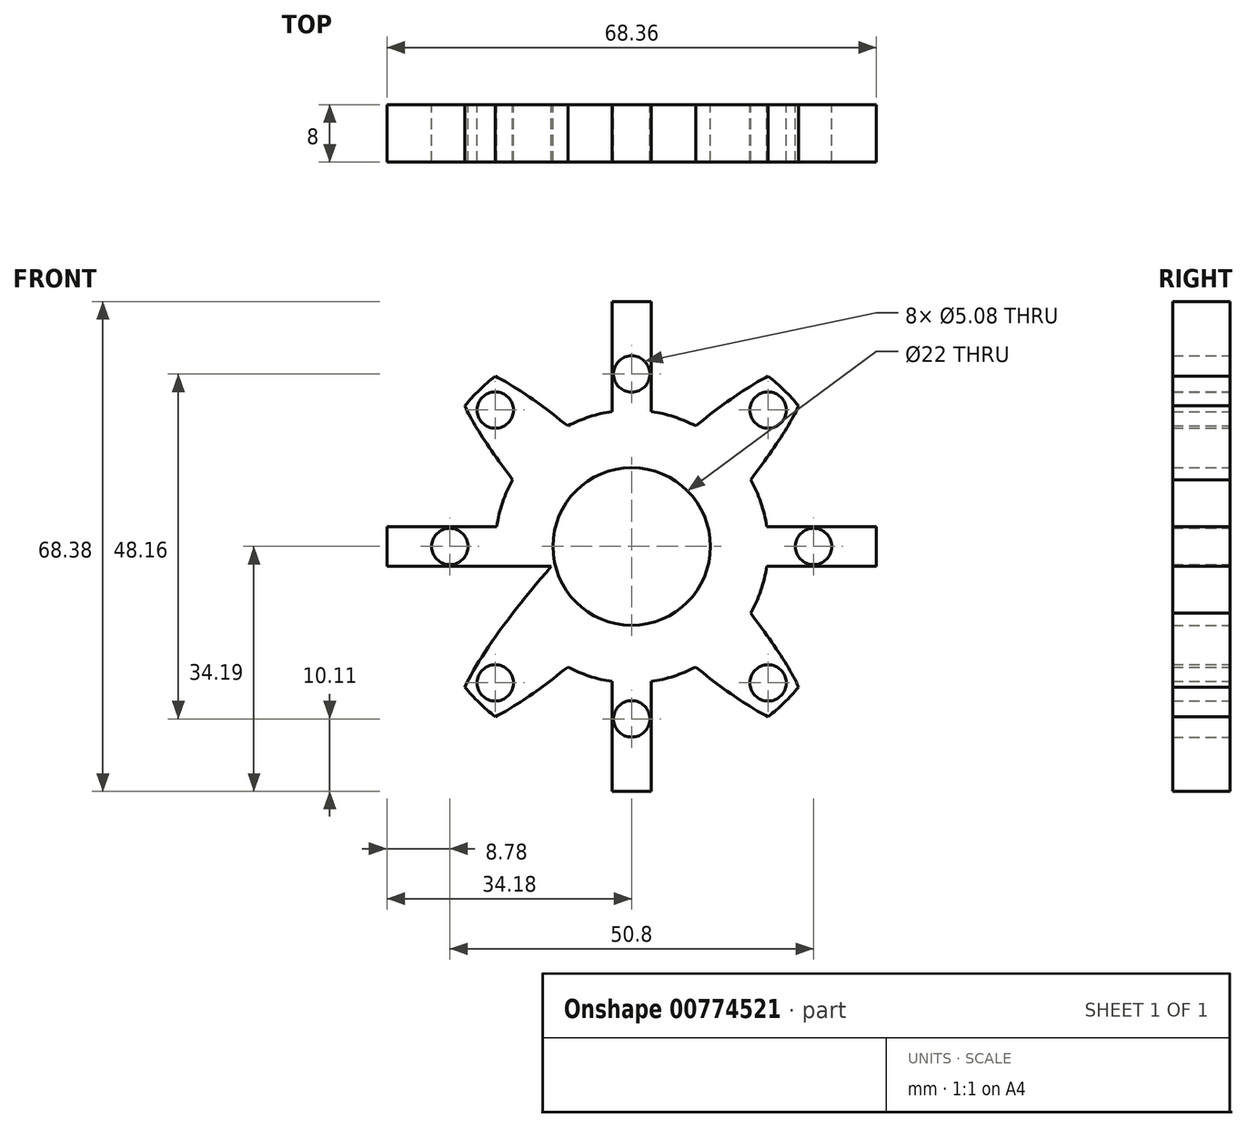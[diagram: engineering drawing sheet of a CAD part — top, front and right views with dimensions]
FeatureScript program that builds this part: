
annotation { "Feature Type Name" : "Feature", "Feature Type Description" : "" }
export const myFeature = defineFeature(function(context is Context, id is Id, definition is map)
    precondition{}
    {
        {
            var Q0;
            Q0=qCreatedBy(makeId("Front.planeOp"),FACE);
            var sketch = newSketch(context, id + "F0", { "sketchPlane" : qUnion([Q0])});
            skPoint(sketch, "E0", {"position": v(-19.05, 19.05) * mm});
            skPoint(sketch, "E1", {"position": v(19.05, 19.05) * mm});
            skPoint(sketch, "E2", {"position": v(19.05, -19.05) * mm});
            skPoint(sketch, "E3", {"position": v(-19.05, -19.05) * mm});
            skPoint(sketch, "E4.middle", {"position": v(0, 0) * mm});
            skPoint(sketch, "E5", {"position": v(-25.4, 0) * mm});
            skPoint(sketch, "E6", {"position": v(25.4, 0) * mm});
            skPoint(sketch, "E7", {"position": v(0, -24.08) * mm});
            skPoint(sketch, "E8", {"position": v(0, 24.08) * mm});
            skCircle(sketch, "E9", {"center": v(0, 0) * mm, "radius": 19.05 * mm});
            skCircle(sketch, "E10", {"center": v(0, 0) * mm, "radius": 34.3 * mm});
            skLineSegment(sketch, "E11.bottom", {"start": v(-2.73, -34.19) * mm, "end": v(2.73, -34.19) * mm});
            skLineSegment(sketch, "E11.top", {"start": v(-2.73, 34.19) * mm, "end": v(2.73, 34.19) * mm});
            skLineSegment(sketch, "E11.left", {"start": v(-2.73, -34.19) * mm, "end": v(-2.73, 34.19) * mm});
            skLineSegment(sketch, "E11.right", {"start": v(2.73, -34.19) * mm, "end": v(2.73, 34.19) * mm});
            skLineSegment(sketch, "E12.bottom", {"start": v(-34.18, -2.78) * mm, "end": v(34.18, -2.78) * mm});
            skLineSegment(sketch, "E12.top", {"start": v(-34.18, 2.78) * mm, "end": v(34.18, 2.78) * mm});
            skLineSegment(sketch, "E12.left", {"start": v(-34.18, -2.78) * mm, "end": v(-34.18, 2.78) * mm});
            skLineSegment(sketch, "E12.right", {"start": v(34.18, -2.78) * mm, "end": v(34.18, 2.78) * mm});
            skPoint(sketch, "E13", {"position": v(-23.96, -24.54) * mm});
            skEllipse(sketch, "E14", {"center": v(0, 0) * mm, "majorRadius": 34.3 * mm, "minorRadius": 6.35 * mm, "majorAxis": v(-0.7, -0.72)});
            skEllipse(sketch, "E15.MirrorC", {"center": v(0, 0) * mm, "majorRadius": 34.3 * mm, "minorRadius": 6.35 * mm, "majorAxis": v(-0.7, 0.72)});
            skCircle(sketch, "E16", {"center": v(0, 0) * mm, "radius": 30.48 * mm});
            skSolve(sketch);
        }
        {
            var Q0;
            {var subQ0=sQuery(id+"F0.wireOp",EDGE,"E11.right");var subQ1=sQuery(id+"F0.wireOp",EDGE,"E9");var subQ2=makeQuery(id+"F0.imprint","INTERSECT",VERTEX,{"disambiguationData":[OD(0.0)],"derivedFrom":[subQ1,subQ0]});Q0=makeQuery(id+"F0.imprint","IMPRINT",FACE,{"disambiguationData":[TD([[makeQuery(id+"F0.imprint","IMPRINT",EDGE,{"disambiguationData":[TD([[subQ2,1.0]])],"derivedFrom":subQ1}),1.0]])]});}
            var Q1;
            {var subQ0=sQuery(id+"F0.wireOp",EDGE,"E11.left");var subQ1=sQuery(id+"F0.wireOp",EDGE,"E9");var subQ2=makeQuery(id+"F0.imprint","INTERSECT",VERTEX,{"disambiguationData":[OD(0.0)],"derivedFrom":[subQ1,subQ0]});Q1=makeQuery(id+"F0.imprint","IMPRINT",FACE,{"disambiguationData":[TD([[makeQuery(id+"F0.imprint","IMPRINT",EDGE,{"disambiguationData":[TD([[subQ2,-1.0]])],"derivedFrom":subQ1}),1.0]])]});}
            var Q2;
            {var subQ0=sQuery(id+"F0.wireOp",EDGE,"E12.bottom");var subQ1=sQuery(id+"F0.wireOp",EDGE,"E9");var subQ2=makeQuery(id+"F0.imprint","INTERSECT",VERTEX,{"disambiguationData":[OD(0.0)],"derivedFrom":[subQ1,subQ0]});Q2=makeQuery(id+"F0.imprint","IMPRINT",FACE,{"disambiguationData":[TD([[makeQuery(id+"F0.imprint","IMPRINT",EDGE,{"disambiguationData":[TD([[subQ2,-1.0]])],"derivedFrom":subQ1}),1.0]])]});}
            var Q3;
            {var subQ0=sQuery(id+"F0.wireOp",EDGE,"E11.right");var subQ1=sQuery(id+"F0.wireOp",EDGE,"E9");var subQ2=makeQuery(id+"F0.imprint","INTERSECT",VERTEX,{"disambiguationData":[OD(1.0)],"derivedFrom":[subQ1,subQ0]});Q3=makeQuery(id+"F0.imprint","IMPRINT",FACE,{"disambiguationData":[TD([[makeQuery(id+"F0.imprint","IMPRINT",EDGE,{"disambiguationData":[TD([[subQ2,-1.0]])],"derivedFrom":subQ1}),1.0]])]});}
            var Q4;
            {var subQ5=sQuery(id+"F0.wireOp",EDGE,"E11.bottom");Q4=makeQuery(id+"F0.imprint","IMPRINT",FACE,{"disambiguationData":[TD([[makeQuery(id+"F0.imprint","IMPRINT",EDGE,{"derivedFrom":subQ5}),1.0]])]});}
            var Q5;
            {var subQ5=sQuery(id+"F0.wireOp",EDGE,"E12.right");Q5=makeQuery(id+"F0.imprint","IMPRINT",FACE,{"disambiguationData":[TD([[makeQuery(id+"F0.imprint","IMPRINT",EDGE,{"derivedFrom":subQ5}),1.0]])]});}
            var Q6;
            {var subQ5=sQuery(id+"F0.wireOp",EDGE,"E11.top");Q6=makeQuery(id+"F0.imprint","IMPRINT",FACE,{"disambiguationData":[TD([[makeQuery(id+"F0.imprint","IMPRINT",EDGE,{"derivedFrom":subQ5}),-1.0]])]});}
            var Q7;
            {var subQ5=sQuery(id+"F0.wireOp",EDGE,"E12.left");Q7=makeQuery(id+"F0.imprint","IMPRINT",FACE,{"disambiguationData":[TD([[makeQuery(id+"F0.imprint","IMPRINT",EDGE,{"derivedFrom":subQ5}),-1.0]])]});}
            var Q8;
            {var subQ0=sQuery(id+"F0.wireOp",EDGE,"E12.top");var subQ1=sQuery(id+"F0.wireOp",EDGE,"E9");var subQ2=makeQuery(id+"F0.imprint","INTERSECT",VERTEX,{"disambiguationData":[OD(1.0)],"derivedFrom":[subQ1,subQ0]});Q8=makeQuery(id+"F0.imprint","IMPRINT",FACE,{"disambiguationData":[TD([[makeQuery(id+"F0.imprint","IMPRINT",EDGE,{"disambiguationData":[TD([[subQ2,-1.0]])],"derivedFrom":subQ1}),1.0]])]});}
            var Q9;
            {var subQ0=sQuery(id+"F0.wireOp",EDGE,"E11.right");var subQ1=sQuery(id+"F0.wireOp",EDGE,"E9");var subQ2=makeQuery(id+"F0.imprint","INTERSECT",VERTEX,{"disambiguationData":[OD(0.0)],"derivedFrom":[subQ1,subQ0]});Q9=makeQuery(id+"F0.imprint","IMPRINT",FACE,{"disambiguationData":[TD([[makeQuery(id+"F0.imprint","IMPRINT",EDGE,{"disambiguationData":[TD([[subQ2,-1.0]])],"derivedFrom":subQ1}),1.0]])]});}
            var Q10;
            {var subQ0=sQuery(id+"F0.wireOp",EDGE,"E12.top");var subQ1=sQuery(id+"F0.wireOp",EDGE,"E9");var subQ2=makeQuery(id+"F0.imprint","INTERSECT",VERTEX,{"disambiguationData":[OD(0.0)],"derivedFrom":[subQ1,subQ0]});Q10=makeQuery(id+"F0.imprint","IMPRINT",FACE,{"disambiguationData":[TD([[makeQuery(id+"F0.imprint","IMPRINT",EDGE,{"disambiguationData":[TD([[subQ2,1.0]])],"derivedFrom":subQ1}),1.0]])]});}
            var Q11;
            {var subQ0=sQuery(id+"F0.wireOp",EDGE,"E11.left");var subQ1=sQuery(id+"F0.wireOp",EDGE,"E9");var subQ2=makeQuery(id+"F0.imprint","INTERSECT",VERTEX,{"disambiguationData":[OD(1.0)],"derivedFrom":[subQ1,subQ0]});Q11=makeQuery(id+"F0.imprint","IMPRINT",FACE,{"disambiguationData":[TD([[makeQuery(id+"F0.imprint","IMPRINT",EDGE,{"disambiguationData":[TD([[subQ2,-1.0]])],"derivedFrom":subQ1}),1.0]])]});}
            var Q12;
            {var subQ0=sQuery(id+"F0.wireOp",EDGE,"E12.bottom");var subQ1=sQuery(id+"F0.wireOp",EDGE,"E11.left");var subQ2=makeQuery(id+"F0.imprint","INTERSECT",VERTEX,{"derivedFrom":[subQ1,subQ0]});Q12=makeQuery(id+"F0.imprint","IMPRINT",FACE,{"disambiguationData":[TD([[makeQuery(id+"F0.imprint","IMPRINT",EDGE,{"disambiguationData":[TD([[subQ2,-1.0]])],"derivedFrom":subQ1}),-1.0]])]});}
            var Q13;
            {var subQ0=sQuery(id+"F0.wireOp",EDGE,"E12.top");var subQ1=sQuery(id+"F0.wireOp",EDGE,"E9");var subQ2=makeQuery(id+"F0.imprint","INTERSECT",VERTEX,{"disambiguationData":[OD(1.0)],"derivedFrom":[subQ1,subQ0]});Q13=makeQuery(id+"F0.imprint","IMPRINT",FACE,{"disambiguationData":[TD([[makeQuery(id+"F0.imprint","IMPRINT",EDGE,{"disambiguationData":[TD([[subQ2,-1.0]])],"derivedFrom":subQ1}),-1.0]])]});}
            var Q14;
            {var subQ0=sQuery(id+"F0.wireOp",EDGE,"E12.top");var subQ1=sQuery(id+"F0.wireOp",EDGE,"E9");var subQ2=makeQuery(id+"F0.imprint","INTERSECT",VERTEX,{"disambiguationData":[OD(0.0)],"derivedFrom":[subQ1,subQ0]});Q14=makeQuery(id+"F0.imprint","IMPRINT",FACE,{"disambiguationData":[TD([[makeQuery(id+"F0.imprint","IMPRINT",EDGE,{"disambiguationData":[TD([[subQ2,1.0]])],"derivedFrom":subQ1}),-1.0]])]});}
            var Q15;
            {var subQ0=sQuery(id+"F0.wireOp",EDGE,"E11.left");var subQ1=sQuery(id+"F0.wireOp",EDGE,"E9");var subQ2=makeQuery(id+"F0.imprint","INTERSECT",VERTEX,{"disambiguationData":[OD(1.0)],"derivedFrom":[subQ1,subQ0]});Q15=makeQuery(id+"F0.imprint","IMPRINT",FACE,{"disambiguationData":[TD([[makeQuery(id+"F0.imprint","IMPRINT",EDGE,{"disambiguationData":[TD([[subQ2,-1.0]])],"derivedFrom":subQ1}),-1.0]])]});}
            var Q16;
            {var subQ0=sQuery(id+"F0.wireOp",EDGE,"E11.right");var subQ1=sQuery(id+"F0.wireOp",EDGE,"E9");var subQ2=makeQuery(id+"F0.imprint","INTERSECT",VERTEX,{"disambiguationData":[OD(0.0)],"derivedFrom":[subQ1,subQ0]});Q16=makeQuery(id+"F0.imprint","IMPRINT",FACE,{"disambiguationData":[TD([[makeQuery(id+"F0.imprint","IMPRINT",EDGE,{"disambiguationData":[TD([[subQ2,-1.0]])],"derivedFrom":subQ1}),-1.0]])]});}
            var Q17;
            {var subQ0=sQuery(id+"F0.wireOp",EDGE,"E11.right");var subQ5=sQuery(id+"F0.wireOp",EDGE,"E10");var subQ6=makeQuery(id+"F0.imprint","INTERSECT",VERTEX,{"disambiguationData":[OD(0.0)],"derivedFrom":[subQ0,subQ5]});Q17=makeQuery(id+"F0.imprint","IMPRINT",FACE,{"disambiguationData":[TD([[makeQuery(id+"F0.imprint","IMPRINT",EDGE,{"disambiguationData":[TD([[subQ6,-1.0]])],"derivedFrom":subQ5}),-1.0]])]});}
            var Q18;
            {var subQ0=sQuery(id+"F0.wireOp",EDGE,"E11.right");var subQ5=sQuery(id+"F0.wireOp",EDGE,"E10");var subQ6=makeQuery(id+"F0.imprint","INTERSECT",VERTEX,{"disambiguationData":[OD(1.0)],"derivedFrom":[subQ0,subQ5]});Q18=makeQuery(id+"F0.imprint","IMPRINT",FACE,{"disambiguationData":[TD([[makeQuery(id+"F0.imprint","IMPRINT",EDGE,{"disambiguationData":[TD([[subQ6,1.0]])],"derivedFrom":subQ5}),-1.0]])]});}
            var Q19;
            {var subQ0=sQuery(id+"F0.wireOp",EDGE,"E11.left");var subQ5=sQuery(id+"F0.wireOp",EDGE,"E10");var subQ6=makeQuery(id+"F0.imprint","INTERSECT",VERTEX,{"disambiguationData":[OD(1.0)],"derivedFrom":[subQ0,subQ5]});Q19=makeQuery(id+"F0.imprint","IMPRINT",FACE,{"disambiguationData":[TD([[makeQuery(id+"F0.imprint","IMPRINT",EDGE,{"disambiguationData":[TD([[subQ6,-1.0]])],"derivedFrom":subQ5}),-1.0]])]});}
            var Q20;
            {var subQ0=sQuery(id+"F0.wireOp",EDGE,"JLvMaHrD-8vfd-X6ZY-ra41-PhhbUremik8w");var subQ1=sQuery(id+"F0.wireOp",EDGE,"E9");var subQ2=makeQuery(id+"F0.imprint","INTERSECT",VERTEX,{"disambiguationData":[OD(1.0)],"derivedFrom":[subQ1,subQ0]});Q20=makeQuery(id+"F0.imprint","IMPRINT",FACE,{"disambiguationData":[TD([[makeQuery(id+"F0.imprint","IMPRINT",EDGE,{"disambiguationData":[TD([[subQ2,-1.0]])],"derivedFrom":subQ1}),1.0]])]});}
            var Q21;
            {var subQ0=sQuery(id+"F0.wireOp",EDGE,"JLvMaHrD-8vfd-X6ZY-ra41-PhhbUremik8w");var subQ1=sQuery(id+"F0.wireOp",EDGE,"E9");var subQ2=makeQuery(id+"F0.imprint","INTERSECT",VERTEX,{"disambiguationData":[OD(0.0)],"derivedFrom":[subQ1,subQ0]});Q21=makeQuery(id+"F0.imprint","IMPRINT",FACE,{"disambiguationData":[TD([[makeQuery(id+"F0.imprint","IMPRINT",EDGE,{"disambiguationData":[TD([[subQ2,-1.0]])],"derivedFrom":subQ1}),-1.0]])]});}
            var Q22;
            {var subQ0=sQuery(id+"F0.wireOp",EDGE,"JLvMaHrD-8vfd-X6ZY-ra41-PhhbUremik8w");var subQ1=sQuery(id+"F0.wireOp",EDGE,"E9");var subQ8=makeQuery(id+"F0.imprint","INTERSECT",VERTEX,{"disambiguationData":[OD(0.0)],"derivedFrom":[subQ1,subQ0]});Q22=makeQuery(id+"F0.imprint","IMPRINT",FACE,{"disambiguationData":[TD([[makeQuery(id+"F0.imprint","IMPRINT",EDGE,{"disambiguationData":[TD([[subQ8,-1.0]])],"derivedFrom":subQ1}),1.0]])]});}
            var Q23;
            {var subQ0=sQuery(id+"F0.wireOp",EDGE,"183bc3bc-c3ae-4ada-a6a3-dfb8a5380e520.MirrorC");var subQ1=sQuery(id+"F0.wireOp",EDGE,"E9");var subQ2=makeQuery(id+"F0.imprint","INTERSECT",VERTEX,{"disambiguationData":[OD(0.0)],"derivedFrom":[subQ1,subQ0]});Q23=makeQuery(id+"F0.imprint","IMPRINT",FACE,{"disambiguationData":[TD([[makeQuery(id+"F0.imprint","IMPRINT",EDGE,{"disambiguationData":[TD([[subQ2,-1.0]])],"derivedFrom":subQ1}),-1.0]])]});}
            var Q24;
            {var subQ0=sQuery(id+"F0.wireOp",EDGE,"JLvMaHrD-8vfd-X6ZY-ra41-PhhbUremik8w");var subQ1=sQuery(id+"F0.wireOp",EDGE,"E9");var subQ2=makeQuery(id+"F0.imprint","INTERSECT",VERTEX,{"disambiguationData":[OD(2.0)],"derivedFrom":[subQ1,subQ0]});Q24=makeQuery(id+"F0.imprint","IMPRINT",FACE,{"disambiguationData":[TD([[makeQuery(id+"F0.imprint","IMPRINT",EDGE,{"disambiguationData":[TD([[subQ2,-1.0]])],"derivedFrom":subQ1}),-1.0]])]});}
            var Q25;
            {var subQ0=sQuery(id+"F0.wireOp",EDGE,"183bc3bc-c3ae-4ada-a6a3-dfb8a5380e520.MirrorC");var subQ1=sQuery(id+"F0.wireOp",EDGE,"E9");var subQ2=makeQuery(id+"F0.imprint","INTERSECT",VERTEX,{"disambiguationData":[OD(2.0)],"derivedFrom":[subQ1,subQ0]});Q25=makeQuery(id+"F0.imprint","IMPRINT",FACE,{"disambiguationData":[TD([[makeQuery(id+"F0.imprint","IMPRINT",EDGE,{"disambiguationData":[TD([[subQ2,-1.0]])],"derivedFrom":subQ1}),-1.0]])]});}
            var Q26;
            {var subQ3=sQuery(id+"F0.wireOp",EDGE,"183bc3bc-c3ae-4ada-a6a3-dfb8a5380e520.MirrorC");var subQ6=sQuery(id+"F0.wireOp",EDGE,"E9");var subQ8=makeQuery(id+"F0.imprint","INTERSECT",VERTEX,{"disambiguationData":[OD(2.0)],"derivedFrom":[subQ6,subQ3]});Q26=makeQuery(id+"F0.imprint","IMPRINT",FACE,{"disambiguationData":[TD([[makeQuery(id+"F0.imprint","IMPRINT",EDGE,{"disambiguationData":[TD([[subQ8,-1.0]])],"derivedFrom":subQ6}),1.0]])]});}
            var Q27;
            {var subQ0=sQuery(id+"F0.wireOp",EDGE,"183bc3bc-c3ae-4ada-a6a3-dfb8a5380e520.MirrorC");var subQ1=sQuery(id+"F0.wireOp",EDGE,"E9");var subQ2=makeQuery(id+"F0.imprint","INTERSECT",VERTEX,{"disambiguationData":[OD(0.0)],"derivedFrom":[subQ1,subQ0]});Q27=makeQuery(id+"F0.imprint","IMPRINT",FACE,{"disambiguationData":[TD([[makeQuery(id+"F0.imprint","IMPRINT",EDGE,{"disambiguationData":[TD([[subQ2,-1.0]])],"derivedFrom":subQ1}),1.0]])]});}
            var Q28;
            {var subQ0=sQuery(id+"F0.wireOp",EDGE,"JLvMaHrD-8vfd-X6ZY-ra41-PhhbUremik8w");var subQ1=sQuery(id+"F0.wireOp",EDGE,"E9");var subQ2=makeQuery(id+"F0.imprint","INTERSECT",VERTEX,{"disambiguationData":[OD(2.0)],"derivedFrom":[subQ1,subQ0]});Q28=makeQuery(id+"F0.imprint","IMPRINT",FACE,{"disambiguationData":[TD([[makeQuery(id+"F0.imprint","IMPRINT",EDGE,{"disambiguationData":[TD([[subQ2,-1.0]])],"derivedFrom":subQ1}),1.0]])]});}
            var Q29;
            {var subQ0=sQuery(id+"F0.wireOp",EDGE,"183bc3bc-c3ae-4ada-a6a3-dfb8a5380e520.MirrorC");var subQ1=sQuery(id+"F0.wireOp",EDGE,"E9");var subQ2=makeQuery(id+"F0.imprint","INTERSECT",VERTEX,{"disambiguationData":[OD(3.0)],"derivedFrom":[subQ1,subQ0]});Q29=makeQuery(id+"F0.imprint","IMPRINT",FACE,{"disambiguationData":[TD([[makeQuery(id+"F0.imprint","IMPRINT",EDGE,{"disambiguationData":[TD([[subQ2,-1.0]])],"derivedFrom":subQ1}),1.0]])]});}
            var Q30;
            {var subQ0=sQuery(id+"F0.wireOp",EDGE,"JLvMaHrD-8vfd-X6ZY-ra41-PhhbUremik8w");var subQ1=sQuery(id+"F0.wireOp",EDGE,"E9");var subQ2=makeQuery(id+"F0.imprint","INTERSECT",VERTEX,{"disambiguationData":[OD(3.0)],"derivedFrom":[subQ1,subQ0]});Q30=makeQuery(id+"F0.imprint","IMPRINT",FACE,{"disambiguationData":[TD([[makeQuery(id+"F0.imprint","IMPRINT",EDGE,{"disambiguationData":[TD([[subQ2,-1.0]])],"derivedFrom":subQ1}),1.0]])]});}
            var Q31;
            {var subQ0=sQuery(id+"F0.wireOp",EDGE,"183bc3bc-c3ae-4ada-a6a3-dfb8a5380e520.MirrorC");var subQ1=sQuery(id+"F0.wireOp",EDGE,"E9");var subQ2=makeQuery(id+"F0.imprint","INTERSECT",VERTEX,{"disambiguationData":[OD(0.0)],"derivedFrom":[subQ1,subQ0]});Q31=makeQuery(id+"F0.imprint","IMPRINT",FACE,{"disambiguationData":[TD([[makeQuery(id+"F0.imprint","IMPRINT",EDGE,{"disambiguationData":[TD([[subQ2,1.0]])],"derivedFrom":subQ1}),1.0]])]});}
            var Q32;
            {var subQ0=sQuery(id+"F0.wireOp",EDGE,"E15.MirrorC");var subQ1=sQuery(id+"F0.wireOp",EDGE,"E9");var subQ2=makeQuery(id+"F0.imprint","INTERSECT",VERTEX,{"disambiguationData":[OD(2.0)],"derivedFrom":[subQ1,subQ0]});Q32=makeQuery(id+"F0.imprint","IMPRINT",FACE,{"disambiguationData":[TD([[makeQuery(id+"F0.imprint","IMPRINT",EDGE,{"disambiguationData":[TD([[subQ2,-1.0]])],"derivedFrom":subQ1}),-1.0]])]});}
            var Q33;
            {var subQ0=sQuery(id+"F0.wireOp",EDGE,"E14");var subQ1=sQuery(id+"F0.wireOp",EDGE,"E9");var subQ2=makeQuery(id+"F0.imprint","INTERSECT",VERTEX,{"disambiguationData":[OD(2.0)],"derivedFrom":[subQ1,subQ0]});Q33=makeQuery(id+"F0.imprint","IMPRINT",FACE,{"disambiguationData":[TD([[makeQuery(id+"F0.imprint","IMPRINT",EDGE,{"disambiguationData":[TD([[subQ2,-1.0]])],"derivedFrom":subQ1}),-1.0]])]});}
            var Q34;
            {var subQ0=sQuery(id+"F0.wireOp",EDGE,"E14");var subQ1=sQuery(id+"F0.wireOp",EDGE,"E9");var subQ2=makeQuery(id+"F0.imprint","INTERSECT",VERTEX,{"disambiguationData":[OD(0.0)],"derivedFrom":[subQ1,subQ0]});Q34=makeQuery(id+"F0.imprint","IMPRINT",FACE,{"disambiguationData":[TD([[makeQuery(id+"F0.imprint","IMPRINT",EDGE,{"disambiguationData":[TD([[subQ2,-1.0]])],"derivedFrom":subQ1}),-1.0]])]});}
            var Q35;
            {var subQ0=sQuery(id+"F0.wireOp",EDGE,"E15.MirrorC");var subQ1=sQuery(id+"F0.wireOp",EDGE,"E9");var subQ2=makeQuery(id+"F0.imprint","INTERSECT",VERTEX,{"disambiguationData":[OD(0.0)],"derivedFrom":[subQ1,subQ0]});Q35=makeQuery(id+"F0.imprint","IMPRINT",FACE,{"disambiguationData":[TD([[makeQuery(id+"F0.imprint","IMPRINT",EDGE,{"disambiguationData":[TD([[subQ2,-1.0]])],"derivedFrom":subQ1}),-1.0]])]});}
            var Q36;
            {var subQ0=sQuery(id+"F0.wireOp",EDGE,"E14");var subQ1=sQuery(id+"F0.wireOp",EDGE,"E9");var subQ2=makeQuery(id+"F0.imprint","INTERSECT",VERTEX,{"disambiguationData":[OD(3.0)],"derivedFrom":[subQ1,subQ0]});Q36=makeQuery(id+"F0.imprint","IMPRINT",FACE,{"disambiguationData":[TD([[makeQuery(id+"F0.imprint","IMPRINT",EDGE,{"disambiguationData":[TD([[subQ2,-1.0]])],"derivedFrom":subQ1}),1.0]])]});}
            var Q37;
            {var subQ0=sQuery(id+"F0.wireOp",EDGE,"E15.MirrorC");var subQ1=sQuery(id+"F0.wireOp",EDGE,"E9");var subQ2=makeQuery(id+"F0.imprint","INTERSECT",VERTEX,{"disambiguationData":[OD(3.0)],"derivedFrom":[subQ1,subQ0]});Q37=makeQuery(id+"F0.imprint","IMPRINT",FACE,{"disambiguationData":[TD([[makeQuery(id+"F0.imprint","IMPRINT",EDGE,{"disambiguationData":[TD([[subQ2,-1.0]])],"derivedFrom":subQ1}),1.0]])]});}
            var Q38;
            {var subQ0=sQuery(id+"F0.wireOp",EDGE,"E14");var subQ1=sQuery(id+"F0.wireOp",EDGE,"E9");var subQ2=makeQuery(id+"F0.imprint","INTERSECT",VERTEX,{"disambiguationData":[OD(0.0)],"derivedFrom":[subQ1,subQ0]});Q38=makeQuery(id+"F0.imprint","IMPRINT",FACE,{"disambiguationData":[TD([[makeQuery(id+"F0.imprint","IMPRINT",EDGE,{"disambiguationData":[TD([[subQ2,1.0]])],"derivedFrom":subQ1}),1.0]])]});}
            var Q39;
            {var subQ0=sQuery(id+"F0.wireOp",EDGE,"E15.MirrorC");var subQ1=sQuery(id+"F0.wireOp",EDGE,"E9");var subQ2=makeQuery(id+"F0.imprint","INTERSECT",VERTEX,{"disambiguationData":[OD(1.0)],"derivedFrom":[subQ1,subQ0]});Q39=makeQuery(id+"F0.imprint","IMPRINT",FACE,{"disambiguationData":[TD([[makeQuery(id+"F0.imprint","IMPRINT",EDGE,{"disambiguationData":[TD([[subQ2,-1.0]])],"derivedFrom":subQ1}),1.0]])]});}
            var Q40;
            {var subQ0=sQuery(id+"F0.wireOp",EDGE,"E14");var subQ1=sQuery(id+"F0.wireOp",EDGE,"E9");var subQ10=makeQuery(id+"F0.imprint","INTERSECT",VERTEX,{"disambiguationData":[OD(2.0)],"derivedFrom":[subQ1,subQ0]});Q40=makeQuery(id+"F0.imprint","IMPRINT",FACE,{"disambiguationData":[TD([[makeQuery(id+"F0.imprint","IMPRINT",EDGE,{"disambiguationData":[TD([[subQ10,-1.0]])],"derivedFrom":subQ1}),1.0]])]});}
            var Q41;
            {var subQ5=sQuery(id+"F0.wireOp",EDGE,"E15.MirrorC");var subQ8=sQuery(id+"F0.wireOp",EDGE,"E9");var subQ9=makeQuery(id+"F0.imprint","INTERSECT",VERTEX,{"disambiguationData":[OD(0.0)],"derivedFrom":[subQ8,subQ5]});Q41=makeQuery(id+"F0.imprint","IMPRINT",FACE,{"disambiguationData":[TD([[makeQuery(id+"F0.imprint","IMPRINT",EDGE,{"disambiguationData":[TD([[subQ9,-1.0]])],"derivedFrom":subQ8}),1.0]])]});}
            var Q42;
            {var subQ0=sQuery(id+"F0.wireOp",EDGE,"E15.MirrorC");var subQ1=sQuery(id+"F0.wireOp",EDGE,"E12.top");var subQ2=makeQuery(id+"F0.imprint","INTERSECT",VERTEX,{"disambiguationData":[OD(0.0)],"derivedFrom":[subQ1,subQ0]});Q42=makeQuery(id+"F0.imprint","IMPRINT",FACE,{"disambiguationData":[TD([[makeQuery(id+"F0.imprint","IMPRINT",EDGE,{"disambiguationData":[TD([[subQ2,-1.0]])],"derivedFrom":subQ1}),-1.0]])]});}
            var Q43;
            {var subQ0=sQuery(id+"F0.wireOp",EDGE,"E14");var subQ1=sQuery(id+"F0.wireOp",EDGE,"E12.bottom");var subQ2=makeQuery(id+"F0.imprint","INTERSECT",VERTEX,{"disambiguationData":[OD(0.0)],"derivedFrom":[subQ1,subQ0]});Q43=makeQuery(id+"F0.imprint","IMPRINT",FACE,{"disambiguationData":[TD([[makeQuery(id+"F0.imprint","IMPRINT",EDGE,{"disambiguationData":[TD([[subQ2,-1.0]])],"derivedFrom":subQ1}),1.0]])]});}
            var Q44;
            {var subQ0=sQuery(id+"F0.wireOp",EDGE,"E14");var subQ1=sQuery(id+"F0.wireOp",EDGE,"E11.left");var subQ2=makeQuery(id+"F0.imprint","INTERSECT",VERTEX,{"disambiguationData":[OD(0.0)],"derivedFrom":[subQ1,subQ0]});Q44=makeQuery(id+"F0.imprint","IMPRINT",FACE,{"disambiguationData":[TD([[makeQuery(id+"F0.imprint","IMPRINT",EDGE,{"disambiguationData":[TD([[subQ2,-1.0]])],"derivedFrom":subQ1}),-1.0]])]});}
            var Q45;
            {var subQ0=sQuery(id+"F0.wireOp",EDGE,"E15.MirrorC");var subQ1=sQuery(id+"F0.wireOp",EDGE,"E11.right");var subQ2=makeQuery(id+"F0.imprint","INTERSECT",VERTEX,{"disambiguationData":[OD(0.0)],"derivedFrom":[subQ1,subQ0]});Q45=makeQuery(id+"F0.imprint","IMPRINT",FACE,{"disambiguationData":[TD([[makeQuery(id+"F0.imprint","IMPRINT",EDGE,{"disambiguationData":[TD([[subQ2,-1.0]])],"derivedFrom":subQ1}),1.0]])]});}
            var Q46;
            {var subQ3=sQuery(id+"F0.wireOp",EDGE,"E15.MirrorC");var subQ6=sQuery(id+"F0.wireOp",EDGE,"E11.left");var subQ9=makeQuery(id+"F0.imprint","INTERSECT",VERTEX,{"disambiguationData":[OD(0.0)],"derivedFrom":[subQ6,subQ3]});Q46=makeQuery(id+"F0.imprint","IMPRINT",FACE,{"disambiguationData":[TD([[makeQuery(id+"F0.imprint","IMPRINT",EDGE,{"disambiguationData":[TD([[subQ9,-1.0]])],"derivedFrom":subQ6}),-1.0]])]});}
            var Q47;
            {var subQ1=sQuery(id+"F0.wireOp",EDGE,"E11.left");var subQ5=sQuery(id+"F0.wireOp",EDGE,"E12.top");var subQ6=makeQuery(id+"F0.imprint","INTERSECT",VERTEX,{"derivedFrom":[subQ1,subQ5]});Q47=makeQuery(id+"F0.imprint","IMPRINT",FACE,{"disambiguationData":[TD([[makeQuery(id+"F0.imprint","IMPRINT",EDGE,{"disambiguationData":[TD([[subQ6,-1.0]])],"derivedFrom":subQ1}),-1.0]])]});}
            var Q48;
            {var subQ1=sQuery(id+"F0.wireOp",EDGE,"E11.left");var subQ5=sQuery(id+"F0.wireOp",EDGE,"E12.bottom");var subQ6=makeQuery(id+"F0.imprint","INTERSECT",VERTEX,{"derivedFrom":[subQ1,subQ5]});Q48=makeQuery(id+"F0.imprint","IMPRINT",FACE,{"disambiguationData":[TD([[makeQuery(id+"F0.imprint","IMPRINT",EDGE,{"disambiguationData":[TD([[subQ6,-1.0]])],"derivedFrom":subQ1}),1.0]])]});}
            var Q49;
            {var subQ1=sQuery(id+"F0.wireOp",EDGE,"E12.bottom");var subQ6=sQuery(id+"F0.wireOp",EDGE,"E11.right");var subQ9=makeQuery(id+"F0.imprint","INTERSECT",VERTEX,{"derivedFrom":[subQ6,subQ1]});Q49=makeQuery(id+"F0.imprint","IMPRINT",FACE,{"disambiguationData":[TD([[makeQuery(id+"F0.imprint","IMPRINT",EDGE,{"disambiguationData":[TD([[subQ9,-1.0]])],"derivedFrom":subQ6}),-1.0]])]});}
            var Q50;
            {var subQ0=sQuery(id+"F0.wireOp",EDGE,"E14");var subQ1=sQuery(id+"F0.wireOp",EDGE,"E11.left");var subQ2=makeQuery(id+"F0.imprint","INTERSECT",VERTEX,{"disambiguationData":[OD(1.0)],"derivedFrom":[subQ1,subQ0]});Q50=makeQuery(id+"F0.imprint","IMPRINT",FACE,{"disambiguationData":[TD([[makeQuery(id+"F0.imprint","IMPRINT",EDGE,{"disambiguationData":[TD([[subQ2,-1.0]])],"derivedFrom":subQ1}),-1.0]])]});}
            var Q51;
            {var subQ0=sQuery(id+"F0.wireOp",EDGE,"E12.top");var subQ1=sQuery(id+"F0.wireOp",EDGE,"E11.left");var subQ2=makeQuery(id+"F0.imprint","INTERSECT",VERTEX,{"derivedFrom":[subQ1,subQ0]});Q51=makeQuery(id+"F0.imprint","IMPRINT",FACE,{"disambiguationData":[TD([[makeQuery(id+"F0.imprint","IMPRINT",EDGE,{"disambiguationData":[TD([[subQ2,-1.0]])],"derivedFrom":subQ1}),1.0]])]});}
            var Q52;
            {var subQ0=sQuery(id+"F0.wireOp",EDGE,"E12.top");var subQ1=sQuery(id+"F0.wireOp",EDGE,"E11.right");var subQ2=makeQuery(id+"F0.imprint","INTERSECT",VERTEX,{"derivedFrom":[subQ1,subQ0]});Q52=makeQuery(id+"F0.imprint","IMPRINT",FACE,{"disambiguationData":[TD([[makeQuery(id+"F0.imprint","IMPRINT",EDGE,{"disambiguationData":[TD([[subQ2,-1.0]])],"derivedFrom":subQ1}),-1.0]])]});}
            var Q53;
            {var subQ0=sQuery(id+"F0.wireOp",EDGE,"E10");var subQ5=sQuery(id+"F0.wireOp",EDGE,"E15.MirrorC");var subQ6=makeQuery(id+"F0.imprint","INTERSECT",VERTEX,{"disambiguationData":[OD(1.0)],"derivedFrom":[subQ0,subQ5]});Q53=makeQuery(id+"F0.imprint","IMPRINT",FACE,{"disambiguationData":[TD([[makeQuery(id+"F0.imprint","IMPRINT",EDGE,{"disambiguationData":[TD([[subQ6,1.0]])],"derivedFrom":subQ5}),-1.0]])]});}
            var Q54;
            {var subQ0=sQuery(id+"F0.wireOp",EDGE,"E10");var subQ5=sQuery(id+"F0.wireOp",EDGE,"E15.MirrorC");var subQ6=makeQuery(id+"F0.imprint","INTERSECT",VERTEX,{"disambiguationData":[OD(1.0)],"derivedFrom":[subQ0,subQ5]});Q54=makeQuery(id+"F0.imprint","IMPRINT",FACE,{"disambiguationData":[TD([[makeQuery(id+"F0.imprint","IMPRINT",EDGE,{"disambiguationData":[TD([[subQ6,-1.0]])],"derivedFrom":subQ5}),-1.0]])]});}
            var Q55;
            {var subQ0=sQuery(id+"F0.wireOp",EDGE,"E14");var subQ1=makeQuery(id+"F0.imprint","INTERSECT",VERTEX,{"disambiguationData":[OD(1.0)],"derivedFrom":[sQuery(id+"F0.wireOp",EDGE,"E10"),subQ0]});Q55=makeQuery(id+"F0.imprint","IMPRINT",FACE,{"disambiguationData":[TD([[makeQuery(id+"F0.imprint","IMPRINT",EDGE,{"disambiguationData":[TD([[subQ1,-1.0]])],"derivedFrom":subQ0}),1.0]])]});}
            var Q56;
            {var subQ0=sQuery(id+"F0.wireOp",EDGE,"E10");var subQ5=sQuery(id+"F0.wireOp",EDGE,"E14");var subQ6=makeQuery(id+"F0.imprint","INTERSECT",VERTEX,{"disambiguationData":[OD(1.0)],"derivedFrom":[subQ0,subQ5]});Q56=makeQuery(id+"F0.imprint","IMPRINT",FACE,{"disambiguationData":[TD([[makeQuery(id+"F0.imprint","IMPRINT",EDGE,{"disambiguationData":[TD([[subQ6,-1.0]])],"derivedFrom":subQ5}),-1.0]])]});}
            var Q57;
            {var subQ0=sQuery(id+"F0.wireOp",EDGE,"E10");var subQ5=sQuery(id+"F0.wireOp",EDGE,"E14");var subQ6=makeQuery(id+"F0.imprint","INTERSECT",VERTEX,{"disambiguationData":[OD(1.0)],"derivedFrom":[subQ0,subQ5]});Q57=makeQuery(id+"F0.imprint","IMPRINT",FACE,{"disambiguationData":[TD([[makeQuery(id+"F0.imprint","IMPRINT",EDGE,{"disambiguationData":[TD([[subQ6,1.0]])],"derivedFrom":subQ5}),-1.0]])]});}
            var Q58;
            {var subQ0=sQuery(id+"F0.wireOp",EDGE,"E10");var subQ5=sQuery(id+"F0.wireOp",EDGE,"E15.MirrorC");var subQ7=makeQuery(id+"F0.imprint","INTERSECT",VERTEX,{"disambiguationData":[OD(0.0)],"derivedFrom":[subQ0,subQ5]});Q58=makeQuery(id+"F0.imprint","IMPRINT",FACE,{"disambiguationData":[TD([[makeQuery(id+"F0.imprint","IMPRINT",EDGE,{"disambiguationData":[TD([[subQ7,-1.0]])],"derivedFrom":subQ5}),-1.0]])]});}
            var Q59;
            {var subQ0=sQuery(id+"F0.wireOp",EDGE,"E15.MirrorC");var subQ1=makeQuery(id+"F0.imprint","INTERSECT",VERTEX,{"disambiguationData":[OD(0.0)],"derivedFrom":[sQuery(id+"F0.wireOp",EDGE,"E10"),subQ0]});Q59=makeQuery(id+"F0.imprint","IMPRINT",FACE,{"disambiguationData":[TD([[makeQuery(id+"F0.imprint","IMPRINT",EDGE,{"disambiguationData":[TD([[subQ1,-1.0]])],"derivedFrom":subQ0}),1.0]])]});}
            var Q60;
            {var subQ0=sQuery(id+"F0.wireOp",EDGE,"E10");var subQ5=sQuery(id+"F0.wireOp",EDGE,"E15.MirrorC");var subQ6=makeQuery(id+"F0.imprint","INTERSECT",VERTEX,{"disambiguationData":[OD(0.0)],"derivedFrom":[subQ0,subQ5]});Q60=makeQuery(id+"F0.imprint","IMPRINT",FACE,{"disambiguationData":[TD([[makeQuery(id+"F0.imprint","IMPRINT",EDGE,{"disambiguationData":[TD([[subQ6,1.0]])],"derivedFrom":subQ5}),-1.0]])]});}
            var Q61;
            {var subQ0=sQuery(id+"F0.wireOp",EDGE,"E10");var subQ5=sQuery(id+"F0.wireOp",EDGE,"E14");var subQ6=makeQuery(id+"F0.imprint","INTERSECT",VERTEX,{"disambiguationData":[OD(0.0)],"derivedFrom":[subQ0,subQ5]});Q61=makeQuery(id+"F0.imprint","IMPRINT",FACE,{"disambiguationData":[TD([[makeQuery(id+"F0.imprint","IMPRINT",EDGE,{"disambiguationData":[TD([[subQ6,-1.0]])],"derivedFrom":subQ5}),-1.0]])]});}
            var Q62;
            {var subQ0=sQuery(id+"F0.wireOp",EDGE,"E14");var subQ1=makeQuery(id+"F0.imprint","INTERSECT",VERTEX,{"disambiguationData":[OD(0.0)],"derivedFrom":[sQuery(id+"F0.wireOp",EDGE,"E10"),subQ0]});Q62=makeQuery(id+"F0.imprint","IMPRINT",FACE,{"disambiguationData":[TD([[makeQuery(id+"F0.imprint","IMPRINT",EDGE,{"disambiguationData":[TD([[subQ1,1.0]])],"derivedFrom":subQ0}),1.0]])]});}
            var Q63;
            {var subQ0=sQuery(id+"F0.wireOp",EDGE,"E10");var subQ5=sQuery(id+"F0.wireOp",EDGE,"E14");var subQ6=makeQuery(id+"F0.imprint","INTERSECT",VERTEX,{"disambiguationData":[OD(0.0)],"derivedFrom":[subQ0,subQ5]});Q63=makeQuery(id+"F0.imprint","IMPRINT",FACE,{"disambiguationData":[TD([[makeQuery(id+"F0.imprint","IMPRINT",EDGE,{"disambiguationData":[TD([[subQ6,1.0]])],"derivedFrom":subQ5}),-1.0]])]});}
            var Q64;
            {var subQ0=sQuery(id+"F0.wireOp",EDGE,"E15.MirrorC");var subQ1=makeQuery(id+"F0.imprint","INTERSECT",VERTEX,{"disambiguationData":[OD(1.0)],"derivedFrom":[sQuery(id+"F0.wireOp",EDGE,"E10"),subQ0]});Q64=makeQuery(id+"F0.imprint","IMPRINT",FACE,{"disambiguationData":[TD([[makeQuery(id+"F0.imprint","IMPRINT",EDGE,{"disambiguationData":[TD([[subQ1,1.0]])],"derivedFrom":subQ0}),1.0]])]});}
            var Q65;
            {var subQ0=sQuery(id+"F0.wireOp",EDGE,"E14");var subQ1=sQuery(id+"F0.wireOp",EDGE,"E11.right");var subQ2=makeQuery(id+"F0.imprint","INTERSECT",VERTEX,{"disambiguationData":[OD(0.0)],"derivedFrom":[subQ1,subQ0]});Q65=makeQuery(id+"F0.imprint","IMPRINT",FACE,{"disambiguationData":[TD([[makeQuery(id+"F0.imprint","IMPRINT",EDGE,{"disambiguationData":[TD([[subQ2,-1.0]])],"derivedFrom":subQ1}),-1.0]])]});}
            var Q66;
            {var subQ5=sQuery(id+"F0.wireOp",EDGE,"E15.MirrorC");var subQ8=sQuery(id+"F0.wireOp",EDGE,"E9");var subQ9=makeQuery(id+"F0.imprint","INTERSECT",VERTEX,{"disambiguationData":[OD(2.0)],"derivedFrom":[subQ8,subQ5]});Q66=makeQuery(id+"F0.imprint","IMPRINT",FACE,{"disambiguationData":[TD([[makeQuery(id+"F0.imprint","IMPRINT",EDGE,{"disambiguationData":[TD([[subQ9,-1.0]])],"derivedFrom":subQ8}),1.0]])]});}
            var Q67;
            {var subQ0=sQuery(id+"F0.wireOp",EDGE,"E15.MirrorC");var subQ1=sQuery(id+"F0.wireOp",EDGE,"E11.left");var subQ2=makeQuery(id+"F0.imprint","INTERSECT",VERTEX,{"disambiguationData":[OD(0.0)],"derivedFrom":[subQ1,subQ0]});Q67=makeQuery(id+"F0.imprint","IMPRINT",FACE,{"disambiguationData":[TD([[makeQuery(id+"F0.imprint","IMPRINT",EDGE,{"disambiguationData":[TD([[subQ2,-1.0]])],"derivedFrom":subQ1}),1.0]])]});}
            var Q68;
            {var subQ0=sQuery(id+"F0.wireOp",EDGE,"E14");var subQ1=sQuery(id+"F0.wireOp",EDGE,"E12.bottom");var subQ2=makeQuery(id+"F0.imprint","INTERSECT",VERTEX,{"disambiguationData":[OD(1.0)],"derivedFrom":[subQ1,subQ0]});Q68=makeQuery(id+"F0.imprint","IMPRINT",FACE,{"disambiguationData":[TD([[makeQuery(id+"F0.imprint","IMPRINT",EDGE,{"disambiguationData":[TD([[subQ2,-1.0]])],"derivedFrom":subQ1}),1.0]])]});}
            var Q69;
            {var subQ0=sQuery(id+"F0.wireOp",EDGE,"E15.MirrorC");var subQ1=sQuery(id+"F0.wireOp",EDGE,"E12.top");var subQ2=makeQuery(id+"F0.imprint","INTERSECT",VERTEX,{"disambiguationData":[OD(1.0)],"derivedFrom":[subQ1,subQ0]});Q69=makeQuery(id+"F0.imprint","IMPRINT",FACE,{"disambiguationData":[TD([[makeQuery(id+"F0.imprint","IMPRINT",EDGE,{"disambiguationData":[TD([[subQ2,-1.0]])],"derivedFrom":subQ1}),-1.0]])]});}
            var Q70;
            {var subQ0=sQuery(id+"F0.wireOp",EDGE,"E14");var subQ1=sQuery(id+"F0.wireOp",EDGE,"E9");var subQ2=makeQuery(id+"F0.imprint","INTERSECT",VERTEX,{"disambiguationData":[OD(0.0)],"derivedFrom":[subQ1,subQ0]});Q70=makeQuery(id+"F0.imprint","IMPRINT",FACE,{"disambiguationData":[TD([[makeQuery(id+"F0.imprint","IMPRINT",EDGE,{"disambiguationData":[TD([[subQ2,-1.0]])],"derivedFrom":subQ1}),1.0]])]});}
            var Q71;
            {var subQ0=sQuery(id+"F0.wireOp",EDGE,"E15.MirrorC");var subQ1=sQuery(id+"F0.wireOp",EDGE,"E11.right");var subQ2=makeQuery(id+"F0.imprint","INTERSECT",VERTEX,{"disambiguationData":[OD(1.0)],"derivedFrom":[subQ1,subQ0]});Q71=makeQuery(id+"F0.imprint","IMPRINT",FACE,{"disambiguationData":[TD([[makeQuery(id+"F0.imprint","IMPRINT",EDGE,{"disambiguationData":[TD([[subQ2,-1.0]])],"derivedFrom":subQ1}),1.0]])]});}
            extrude(context, id + "F1", {"entities" : qUnion([Q0, Q1, Q2, Q3, Q4, Q5, Q6, Q7, Q8, Q9, Q10, Q11, Q12, Q13, Q14, Q15, Q16, Q17, Q18, Q19, Q20, Q21, Q22, Q23, Q24, Q25, Q26, Q27, Q28, Q29, Q30, Q31, Q32, Q33, Q34, Q35, Q36, Q37, Q38, Q39, Q40, Q41, Q42, Q43, Q44, Q45, Q46, Q47, Q48, Q49, Q50, Q51, Q52, Q53, Q54, Q55, Q56, Q57, Q58, Q59, Q60, Q61, Q62, Q63, Q64, Q65, Q66, Q67, Q68, Q69, Q70, Q71]), "depth" : 8 * mm, "offsetDistance" : 25.4 * mm});
        }
        {
            var Q0;
            Q0=sQuery(id+"F0.wireOp",VERTEX,"E4.middle");
            var Q1;
            Q1=makeQuery(id+"F1.opExtrude","SWEPT_BODY",BODY,{"disambiguationData":[OSD([sQuery(id+"F0.wireOp",EDGE,"E9")])]});
            hole(context, id + "F2", {"style" : HoleStyle.SIMPLE, "endStyle" : HoleEndStyle.THROUGH, "oppositeDirection" : true, "holeDiameter" : 22 * mm, "majorDiameter" : 6.35 * mm, "isTappedThrough" : true, "tappedDepth" : 12.7 * mm, "tapClearance" : 3, "locations" : qUnion([Q0]), "scope" : qUnion([Q1])});
        }
        {
            var Q0;
            Q0=sQuery(id+"F0.wireOp",VERTEX,"E5");
            var Q1;
            Q1=sQuery(id+"F0.wireOp",VERTEX,"E8");
            var Q2;
            Q2=sQuery(id+"F0.wireOp",VERTEX,"E6");
            var Q3;
            Q3=sQuery(id+"F0.wireOp",VERTEX,"E7");
            var Q4;
            Q4=sQuery(id+"F0.wireOp",VERTEX,"E0");
            var Q5;
            Q5=sQuery(id+"F0.wireOp",VERTEX,"E1");
            var Q6;
            Q6=sQuery(id+"F0.wireOp",VERTEX,"E2");
            var Q7;
            Q7=sQuery(id+"F0.wireOp",VERTEX,"E3");
            var Q8;
            Q8=makeQuery(id+"F1.opExtrude","SWEPT_BODY",BODY,{"disambiguationData":[OSD([sQuery(id+"F0.wireOp",EDGE,"E9"),sQuery(id+"F0.wireOp",EDGE,"E10"),sQuery(id+"F0.wireOp",EDGE,"E11.bottom"),sQuery(id+"F0.wireOp",EDGE,"E11.top"),sQuery(id+"F0.wireOp",EDGE,"E11.left"),sQuery(id+"F0.wireOp",EDGE,"E11.right"),sQuery(id+"F0.wireOp",EDGE,"E12.bottom"),sQuery(id+"F0.wireOp",EDGE,"E12.top"),sQuery(id+"F0.wireOp",EDGE,"E12.left"),sQuery(id+"F0.wireOp",EDGE,"E12.right"),sQuery(id+"F0.wireOp",EDGE,"E10")])]});
            hole(context, id + "F3", {"style" : HoleStyle.SIMPLE, "endStyle" : HoleEndStyle.THROUGH, "oppositeDirection" : true, "holeDiameter" : 5.08 * mm, "majorDiameter" : 6.35 * mm, "isTappedThrough" : true, "tappedDepth" : 12.7 * mm, "tapClearance" : 3, "locations" : qUnion([Q0, Q1, Q2, Q3, Q4, Q5, Q6, Q7]), "scope" : qUnion([Q8])});
        }
    });
